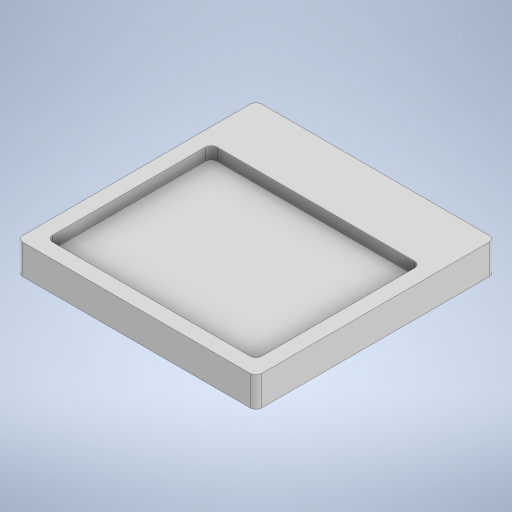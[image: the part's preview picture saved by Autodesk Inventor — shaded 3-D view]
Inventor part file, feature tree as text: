
AUTODESK INVENTOR PART (.ipt)
format: ipt  version: 2023 (Build 270158000, 158)  size: 262,144 bytes
history: native  units: mm
features: extrude x2, fillet x2, sketch x2
ambient origin geometry x8: Origin, YZ Plane, XZ Plane, XY Plane, X Axis, Y Axis, Z Axis, Center Point
bodies: Solid1 (feature_tree)
feature tree (6):
  extrude  "Extrusion1"  Depth=80.0mm
  extrude  "Extrusion2"  Depth=70.0mm
  fillet  "Fillet1"  Radius=55.0mm
  fillet  "Fillet2"  Radius=5.0mm
  sketch  "Sketch1"  dims[d0=80.0mm d1=80.0mm]
  sketch  "Sketch2"  dims[d6=6.0mm d7=0.0mm d8=70.0mm d9=55.0mm d10=5.0mm d11=5.0mm d12=4.0mm d13=0.0mm d14=2.0mm d15=2.0mm d16=0.0mm d17=0.0mm]
